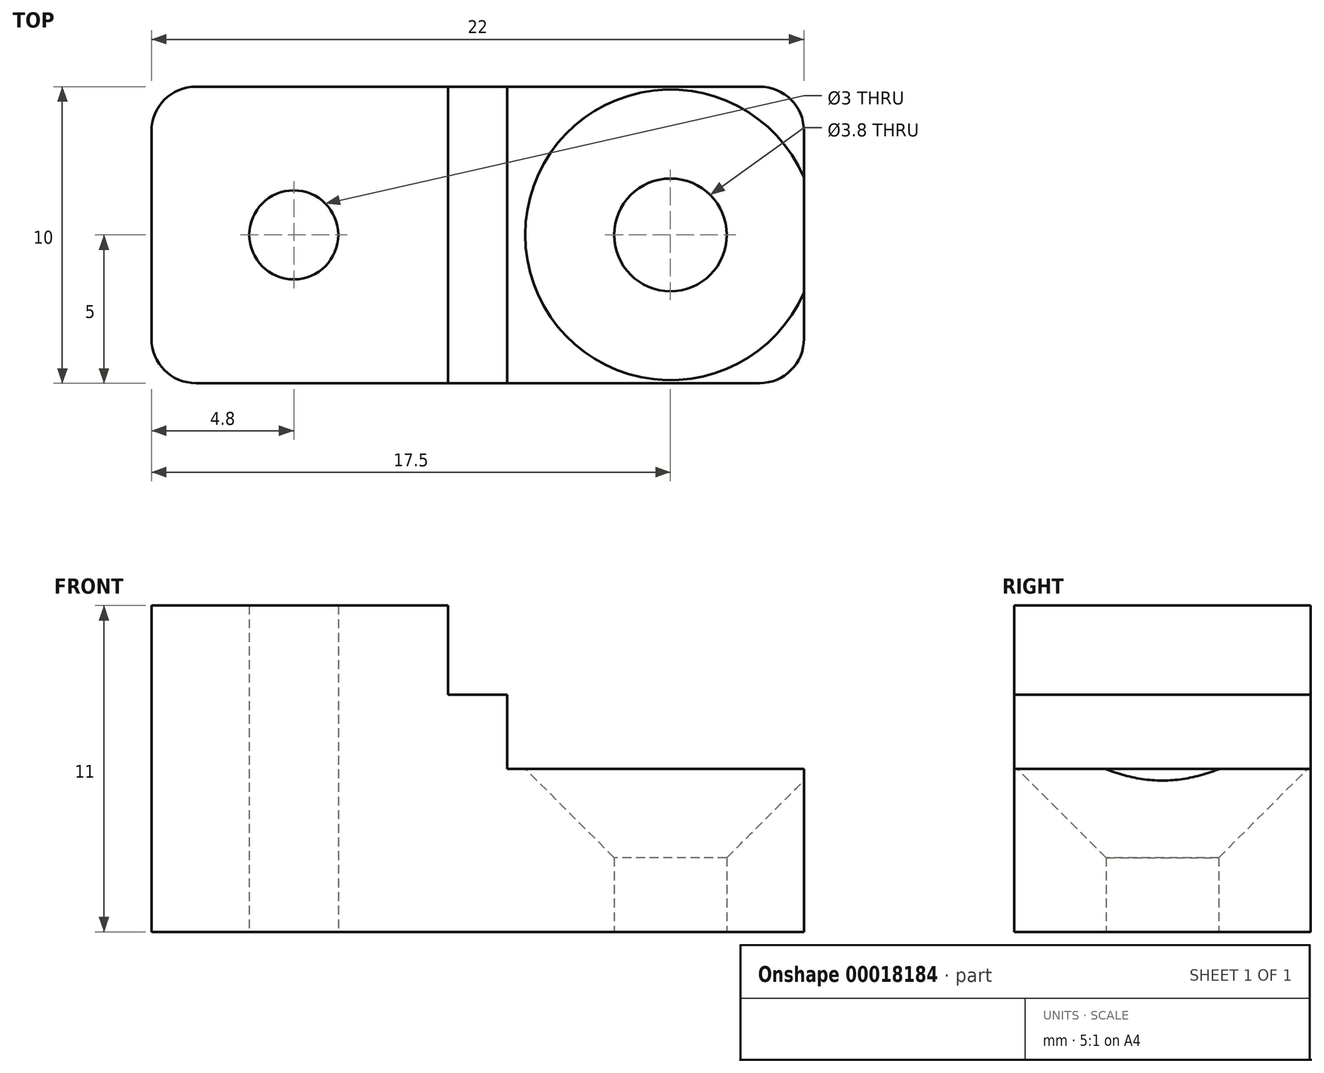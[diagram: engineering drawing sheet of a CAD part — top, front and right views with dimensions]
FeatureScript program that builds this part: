
annotation { "Feature Type Name" : "Feature", "Feature Type Description" : "" }
export const myFeature = defineFeature(function(context is Context, id is Id, definition is map)
    precondition{}
    {
        {
            var Q0;
            Q0=qCreatedBy(makeId("Top.planeOp"),FACE);
            var sketch = newSketch(context, id + "F0", { "sketchPlane" : qUnion([Q0])});
            skLineSegment(sketch, "E0.bottom", {"start": v(-1.5, 0) * mm, "end": v(-20.5, 0) * mm});
            skLineSegment(sketch, "E0.top", {"start": v(-1.5, 10) * mm, "end": v(-20.5, 10) * mm});
            skLineSegment(sketch, "E0.left", {"start": v(0, 1.5) * mm, "end": v(0, 8.5) * mm});
            skLineSegment(sketch, "E0.right", {"start": v(-22, 1.5) * mm, "end": v(-22, 8.5) * mm});
            skPoint(sketch, "E1.visualSharp", {"position": v(-22, 10) * mm});
            skArc(sketch, "E1.filletArc", {"start": v(-20.5, 10) * mm, "mid": v(-21.56, 9.56) * mm, "end": v(-22, 8.5) * mm});
            skPoint(sketch, "E2.visualSharp", {"position": v(0, 10) * mm});
            skArc(sketch, "E2.filletArc", {"start": v(0, 8.5) * mm, "mid": v(-0.44, 9.56) * mm, "end": v(-1.5, 10) * mm});
            skPoint(sketch, "E3.visualSharp", {"position": v(0, 0) * mm});
            skArc(sketch, "E3.filletArc", {"start": v(-1.5, 0) * mm, "mid": v(-0.44, 0.44) * mm, "end": v(0, 1.5) * mm});
            skPoint(sketch, "E4.visualSharp", {"position": v(-22, 0) * mm});
            skArc(sketch, "E4.filletArc", {"start": v(-22, 1.5) * mm, "mid": v(-21.56, 0.44) * mm, "end": v(-20.5, 0) * mm});
            skLineSegment(sketch, "E5", {"start": v(-22, 5) * mm, "end": v(0, 5) * mm, "construction": true});
            skPoint(sketch, "E6", {"position": v(-17.2, 5) * mm});
            skPoint(sketch, "E7", {"position": v(-4.5, 5) * mm});
            skCircle(sketch, "E8", {"center": v(-17.2, 5) * mm, "radius": 1.5 * mm});
            skCircle(sketch, "E9", {"center": v(-4.5, 5) * mm, "radius": 1.9 * mm});
            skLineSegment(sketch, "E10", {"start": v(-12, 10) * mm, "end": v(-12, 0) * mm});
            skLineSegment(sketch, "E11", {"start": v(-10, 10) * mm, "end": v(-10, 0) * mm});
            skSolve(sketch);
        }
        {
            var Q0;
            Q0=makeQuery(id+"F0.imprint","IMPRINT",FACE,{"disambiguationData":[TD([[makeQuery(id+"F0.imprint","IMPRINT",EDGE,{"derivedFrom":sQuery(id+"F0.wireOp",EDGE,"E0.right")}),-1.0]])]});
            extrude(context, id + "F1", {"entities" : qUnion([Q0]), "depth" : 11 * mm});
        }
        {
            var Q0;
            {var subQ1=sQuery(id+"F0.wireOp",EDGE,"E10");Q0=makeQuery(id+"F0.imprint","IMPRINT",FACE,{"disambiguationData":[TD([[makeQuery(id+"F0.imprint","IMPRINT",EDGE,{"derivedFrom":subQ1}),1.0]])]});}
            extrude(context, id + "F2", {"entities" : qUnion([Q0]), "operationType" : NewBodyOperationType.ADD, "depth" : 8 * mm});
        }
        {
            var Q0;
            Q0=makeQuery(id+"F0.imprint","IMPRINT",FACE,{"disambiguationData":[TD([[makeQuery(id+"F0.imprint","IMPRINT",EDGE,{"derivedFrom":sQuery(id+"F0.wireOp",EDGE,"E0.left")}),1.0]])]});
            extrude(context, id + "F3", {"entities" : qUnion([Q0]), "operationType" : NewBodyOperationType.ADD, "depth" : 5.5 * mm});
        }
        {
            var Q0;
            Q0=makeQuery(id+"F3.opExtrude","CAP_EDGE",EDGE,{"disambiguationData":[OSD([sQuery(id+"F0.wireOp",EDGE,"E9")])],"isStart":false});
            chamfer(context, id + "F4", {"entities" : qUnion([Q0]), "width" : 3 * mm, "tangentPropagation" : true});
        }
    });
